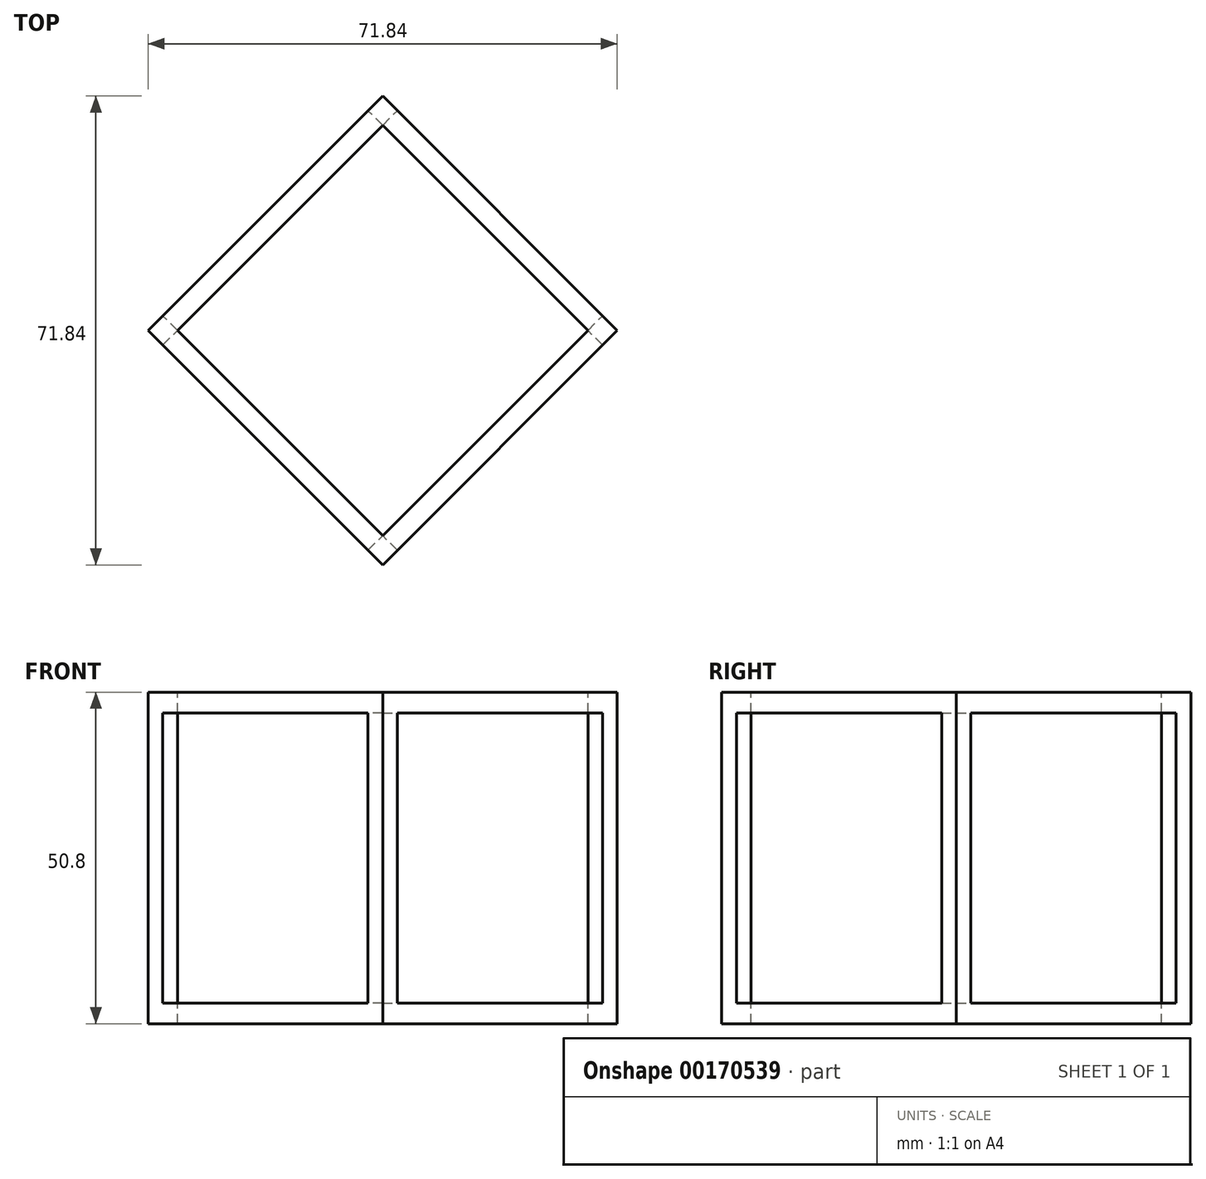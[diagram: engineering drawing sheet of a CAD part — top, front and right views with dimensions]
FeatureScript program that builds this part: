
annotation { "Feature Type Name" : "Feature", "Feature Type Description" : "" }
export const myFeature = defineFeature(function(context is Context, id is Id, definition is map)
    precondition{}
    {
        {
            var Q0;
            Q0=qCreatedBy(makeId("Front.planeOp"),FACE);
            var sketch = newSketch(context, id + "F0", { "sketchPlane" : qUnion([Q0])});
            skLineSegment(sketch, "E0.bottom", {"start": v(-12.7, 12.7) * mm, "end": v(12.7, 12.7) * mm});
            skLineSegment(sketch, "E0.top", {"start": v(-12.7, -12.7) * mm, "end": v(12.7, -12.7) * mm});
            skLineSegment(sketch, "E0.left", {"start": v(-12.7, 12.7) * mm, "end": v(-12.7, -12.7) * mm});
            skLineSegment(sketch, "E0.right", {"start": v(12.7, 12.7) * mm, "end": v(12.7, -12.7) * mm});
            skLineSegment(sketch, "E1.bottom", {"start": v(-9.53, 9.53) * mm, "end": v(9.53, 9.53) * mm});
            skLineSegment(sketch, "E1.top", {"start": v(-9.53, -9.53) * mm, "end": v(9.53, -9.53) * mm});
            skLineSegment(sketch, "E1.left", {"start": v(-9.53, 9.53) * mm, "end": v(-9.53, -9.53) * mm});
            skLineSegment(sketch, "E1.right", {"start": v(9.53, 9.53) * mm, "end": v(9.53, -9.53) * mm});
            skSolve(sketch);
        }
        {
            var Q0;
            Q0 = qSketchRegion(id + "F0", true);
            extrude(context, id + "F1", {"entities" : qUnion([Q0]), "endBound" : BoundingType.SYMMETRIC, "depth" : 25.4 * mm});
        }
        {
            var Q0;
            Q0=makeQuery(id+"F1.opExtrude","SWEPT_FACE",FACE,{"disambiguationData":[OSD([sQuery(id+"F0.wireOp",EDGE,"E0.right")])]});
            var sketch = newSketch(context, id + "F2", { "sketchPlane" : qUnion([Q0])});
            skLineSegment(sketch, "E2.bottom", {"start": v(-9.53, 9.53) * mm, "end": v(9.53, 9.53) * mm});
            skLineSegment(sketch, "E2.top", {"start": v(-9.53, -9.53) * mm, "end": v(9.52, -9.53) * mm});
            skLineSegment(sketch, "E2.left", {"start": v(-9.53, 9.52) * mm, "end": v(-9.53, -9.53) * mm});
            skLineSegment(sketch, "E2.right", {"start": v(9.53, 9.53) * mm, "end": v(9.53, -9.53) * mm});
            skSolve(sketch);
        }
        {
            var Q0;
            Q0 = qSketchRegion(id + "F2", true);
            extrude(context, id + "F3", {"entities" : qUnion([Q0]), "operationType" : NewBodyOperationType.REMOVE, "oppositeDirection" : true, "depth" : 25.4 * mm});
        }
        {
            var Q0;
            Q0=makeQuery(id+"F1.opExtrude","SWEPT_FACE",FACE,{"disambiguationData":[OSD([sQuery(id+"F0.wireOp",EDGE,"E0.bottom")])]});
            var sketch = newSketch(context, id + "F4", { "sketchPlane" : qUnion([Q0])});
            skLineSegment(sketch, "E3.bottom", {"start": v(-9.65, 9.53) * mm, "end": v(9.53, 9.53) * mm});
            skLineSegment(sketch, "E3.top", {"start": v(-9.65, -9.53) * mm, "end": v(9.53, -9.53) * mm});
            skLineSegment(sketch, "E3.left", {"start": v(-9.65, 9.53) * mm, "end": v(-9.65, -9.53) * mm});
            skLineSegment(sketch, "E3.right", {"start": v(9.53, 9.53) * mm, "end": v(9.53, -9.53) * mm});
            skSolve(sketch);
        }
        {
            var Q0;
            Q0 = qSketchRegion(id + "F4", true);
            var Q1;
            Q1=makeQuery(id+"F1.opExtrude","SWEPT_FACE",FACE,{"disambiguationData":[OSD([sQuery(id+"F0.wireOp",EDGE,"E0.top")])]});
            extrude(context, id + "F5", {"entities" : qUnion([Q0]), "operationType" : NewBodyOperationType.REMOVE, "endBound" : BoundingType.UP_TO_SURFACE, "oppositeDirection" : true, "endBoundEntityFace" : qUnion([Q1]), "depth" : 25.4 * mm});
        }
        {
            var Q0;
            Q0=makeQuery(id+"F1.opExtrude","CAP_VERTEX",VERTEX,{"disambiguationData":[OSD([sQuery(id+"F0.wireOp",EDGE,"E0.bottom"),sQuery(id+"F0.wireOp",EDGE,"E0.left")])],"isStart":true});
            var Q1;
            Q1=makeQuery(id+"F1.opExtrude","CAP_EDGE",EDGE,{"disambiguationData":[OSD([sQuery(id+"F0.wireOp",EDGE,"E0.right")])],"isStart":false});
            cPlane(context, id + "F6", {"entities" : qUnion([Q0, Q1]), "cplaneType" : CPlaneType.LINE_ANGLE, "offset" : 25.4 * mm, "angle" : 180 * degree, "width" : 152.4 * mm, "height" : 152.4 * mm});
        }
        {
            var Q0;
            Q0=qCreatedBy(id+"F6.planeOp",FACE);
            var sketch = newSketch(context, id + "F7", { "sketchPlane" : qUnion([Q0])});
            skLineSegment(sketch, "E4.bottom", {"start": v(-25.4, 25.4) * mm, "end": v(25.4, 25.4) * mm});
            skLineSegment(sketch, "E4.top", {"start": v(-25.4, -25.4) * mm, "end": v(25.4, -25.4) * mm});
            skLineSegment(sketch, "E4.left", {"start": v(-25.4, 25.4) * mm, "end": v(-25.4, -25.4) * mm});
            skLineSegment(sketch, "E4.right", {"start": v(25.4, 25.4) * mm, "end": v(25.4, -25.4) * mm});
            skLineSegment(sketch, "E5.0", {"start": v(-22.23, 22.23) * mm, "end": v(22.23, 22.23) * mm});
            skLineSegment(sketch, "E5.1", {"start": v(-22.23, 22.23) * mm, "end": v(-22.23, -22.23) * mm});
            skLineSegment(sketch, "E5.2", {"start": v(-22.23, -22.23) * mm, "end": v(22.23, -22.23) * mm});
            skLineSegment(sketch, "E5.3", {"start": v(22.23, 22.23) * mm, "end": v(22.23, -22.23) * mm});
            skSolve(sketch);
        }
        {
            var Q0;
            Q0 = qSketchRegion(id + "F7", true);
            extrude(context, id + "F8", {"entities" : qUnion([Q0]), "endBound" : BoundingType.SYMMETRIC, "depth" : 50.8 * mm});
        }
        {
            var Q0;
            Q0=makeQuery(id+"F8.opExtrude","SWEPT_FACE",FACE,{"disambiguationData":[OSD([sQuery(id+"F7.wireOp",EDGE,"E4.left")])]});
            var sketch = newSketch(context, id + "F9", { "sketchPlane" : qUnion([Q0])});
            skLineSegment(sketch, "E6.bottom", {"start": v(-22.23, 22.23) * mm, "end": v(22.23, 22.23) * mm});
            skLineSegment(sketch, "E6.top", {"start": v(-22.22, -22.22) * mm, "end": v(22.23, -22.22) * mm});
            skLineSegment(sketch, "E6.left", {"start": v(-22.23, 22.23) * mm, "end": v(-22.22, -22.22) * mm});
            skLineSegment(sketch, "E6.right", {"start": v(22.23, 22.23) * mm, "end": v(22.23, -22.22) * mm});
            skSolve(sketch);
        }
        {
            var Q0;
            Q0 = qSketchRegion(id + "F9", true);
            extrude(context, id + "F10", {"entities" : qUnion([Q0]), "operationType" : NewBodyOperationType.REMOVE, "endBound" : BoundingType.THROUGH_ALL, "oppositeDirection" : true, "depth" : 25.4 * mm});
        }
        {
            var Q0;
            Q0=makeQuery(id+"F8.opExtrude","SWEPT_FACE",FACE,{"disambiguationData":[OSD([sQuery(id+"F7.wireOp",EDGE,"E4.bottom")])]});
            var sketch = newSketch(context, id + "F11", { "sketchPlane" : qUnion([Q0])});
            skLineSegment(sketch, "E7", {"start": v(0, 31.43) * mm, "end": v(-31.43, 0) * mm});
            skLineSegment(sketch, "E8", {"start": v(-31.43, 0) * mm, "end": v(0, -31.43) * mm});
            skLineSegment(sketch, "E9", {"start": v(0, 31.43) * mm, "end": v(31.43, 0) * mm});
            skLineSegment(sketch, "E10", {"start": v(31.43, 0) * mm, "end": v(0, -31.43) * mm});
            skSolve(sketch);
        }
        {
            var Q0;
            Q0 = qSketchRegion(id + "F11", true);
            extrude(context, id + "F12", {"entities" : qUnion([Q0]), "operationType" : NewBodyOperationType.REMOVE, "endBound" : BoundingType.THROUGH_ALL, "oppositeDirection" : true, "depth" : 25.4 * mm});
        }
    });
